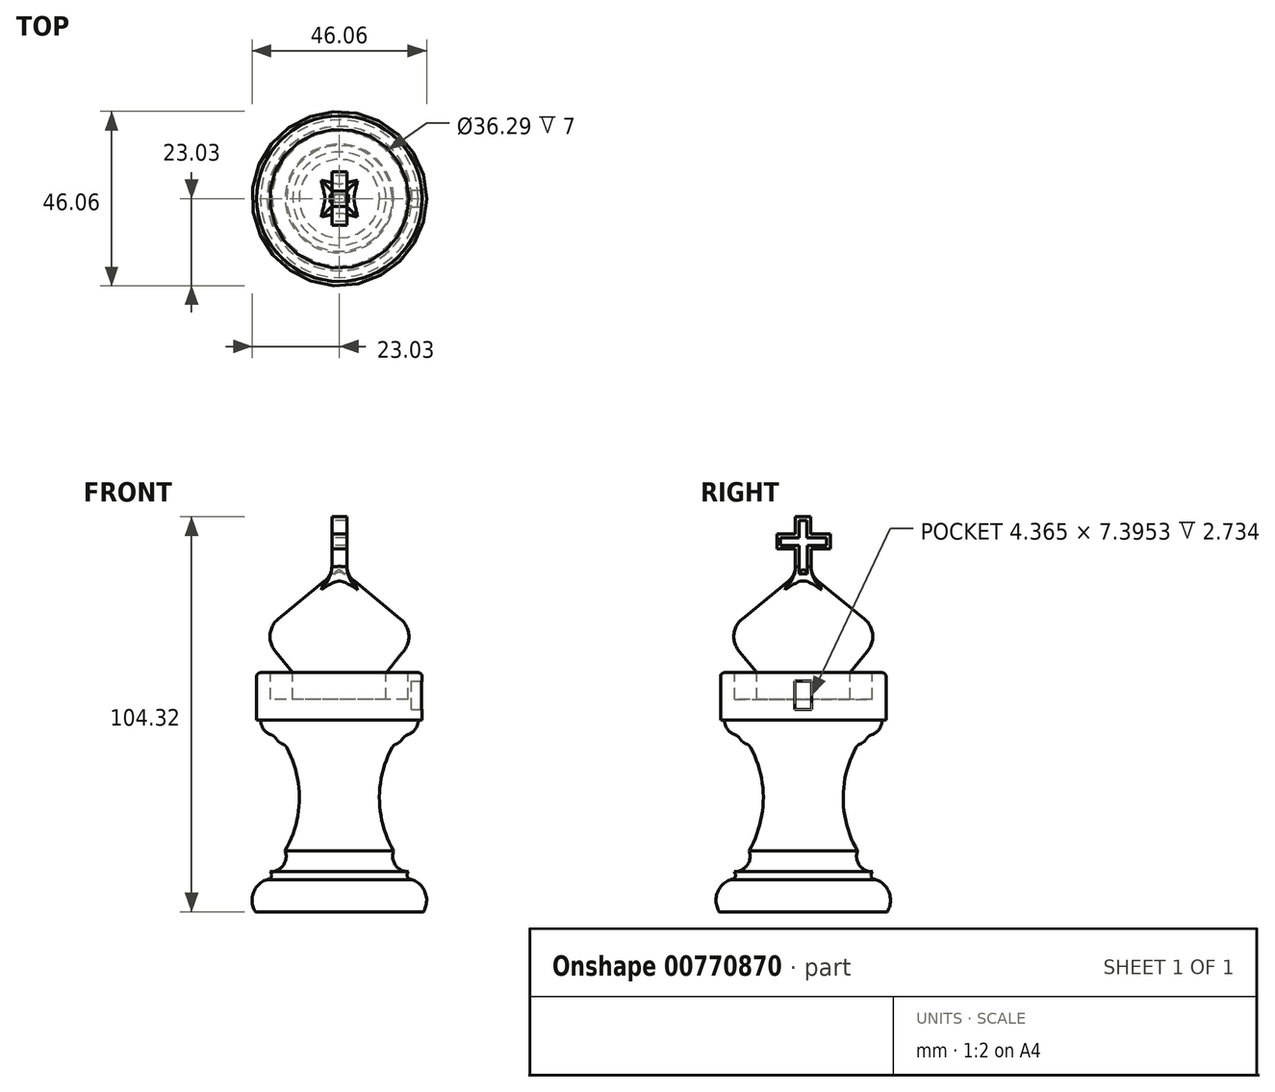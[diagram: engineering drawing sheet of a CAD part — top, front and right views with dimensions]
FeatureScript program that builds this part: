
annotation { "Feature Type Name" : "Feature", "Feature Type Description" : "" }
export const myFeature = defineFeature(function(context is Context, id is Id, definition is map)
    precondition{}
    {
        {
            var Q0;
            Q0=qCreatedBy(makeId("Front.planeOp"),FACE);
            var sketch = newSketch(context, id + "F0", { "sketchPlane" : qUnion([Q0])});
            skLineSegment(sketch, "E0.bottom", {"start": v(0, 0) * mm, "end": v(22.16, 0) * mm});
            skLineSegment(sketch, "E0.top", {"start": v(19.04, 8.54) * mm, "end": v(19.04, 8.54) * mm});
            skLineSegment(sketch, "E1.bottom", {"start": v(19.04, 8.54) * mm, "end": v(19.08, 8.54) * mm});
            skLineSegment(sketch, "E2.bottom", {"start": v(20.81, 50.62) * mm, "end": v(21.84, 50.62) * mm});
            skLineSegment(sketch, "E2.top", {"start": v(12.33, 63.15) * mm, "end": v(21.84, 63.15) * mm});
            skLineSegment(sketch, "E2.right", {"start": v(21.84, 50.62) * mm, "end": v(21.84, 63.15) * mm});
            skLineSegment(sketch, "E3.bottom", {"start": v(12.33, 63.15) * mm, "end": v(20.81, 63.15) * mm});
            skArc(sketch, "E4", {"start": v(14.33, 44.14) * mm, "mid": v(10.55, 30.13) * mm, "end": v(14.33, 16.12) * mm});
            skPoint(sketch, "E5.orphan", {"position": v(9.96, 63.15) * mm});
            skArc(sketch, "E6", {"start": v(18.27, 10.6) * mm, "mid": v(17.95, 9.3) * mm, "end": v(19.04, 8.54) * mm});
            skArc(sketch, "E7", {"start": v(22.16, 0) * mm, "mid": v(22.7, 5.01) * mm, "end": v(19.08, 8.54) * mm});
            skArc(sketch, "E8", {"start": v(14.33, 16.12) * mm, "mid": v(14.82, 12.3) * mm, "end": v(18.27, 10.6) * mm});
            skArc(sketch, "E9", {"start": v(14.33, 44.14) * mm, "mid": v(16.06, 44.95) * mm, "end": v(17.1, 46.54) * mm});
            skArc(sketch, "E10", {"start": v(17.1, 46.54) * mm, "mid": v(19.74, 47.86) * mm, "end": v(20.81, 50.62) * mm});
            skLineSegment(sketch, "E11", {"start": v(0, 90.54) * mm, "end": v(16.13, 77.37) * mm});
            skLineSegment(sketch, "E12", {"start": v(16.99, 68.86) * mm, "end": v(12.33, 63.15) * mm});
            skPoint(sketch, "E13.visualSharp", {"position": v(20.81, 73.55) * mm});
            skArc(sketch, "E13.filletArc", {"start": v(16.99, 68.86) * mm, "mid": v(18.32, 73.3) * mm, "end": v(16.13, 77.37) * mm});
            skPoint(sketch, "E14.orphan", {"position": v(20.81, 83.94) * mm});
            skLineSegment(sketch, "E15", {"start": v(0, 90.54) * mm, "end": v(0, 0) * mm});
            skSolve(sketch);
        }
        {
            var Q0;
            Q0=makeQuery(id+"F0.imprint","IMPRINT",FACE,{"disambiguationData":[TD([[makeQuery(id+"F0.imprint","IMPRINT",EDGE,{"derivedFrom":sQuery(id+"F0.wireOp",EDGE,"E0.bottom")}),1.0]])]});
            var Q1;
            Q1=sQuery(id+"F0.wireOp",EDGE,"E15");
            revolve(context, id + "F1", {"surfaceOperationType" : NewSurfaceOperationType.NEW, "entities" : qUnion([Q0]), "axis" : qUnion([Q1]), "revolveType" : RevolveType.FULL});
        }
        {
            var Q0;
            Q0=makeQuery(id+"F1.opRevolve","SWEPT_EDGE",EDGE,{"disambiguationData":[OSD([sQuery(id+"F0.wireOp",EDGE,"E4"),sQuery(id+"F0.wireOp",EDGE,"E9")])]});
            fillet(context, id + "F2", {"entities" : qUnion([Q0]), "radius" : 2 * mm, "tangentPropagation" : true, "allowEdgeOverflow" : false});
        }
        {
            var Q0;
            Q0=makeQuery(id+"F1.opRevolve","SWEPT_EDGE",EDGE,{"disambiguationData":[OSD([sQuery(id+"F0.wireOp",EDGE,"E9"),sQuery(id+"F0.wireOp",EDGE,"E10")])]});
            fillet(context, id + "F3", {"entities" : qUnion([Q0]), "radius" : 2 * mm, "tangentPropagation" : true, "allowEdgeOverflow" : false});
        }
        {
            var Q0;
            Q0=makeQuery(id+"F1.opRevolve","SWEPT_FACE",FACE,{"disambiguationData":[OSD([sQuery(id+"F0.wireOp",EDGE,"E2.top"),sQuery(id+"F0.wireOp",EDGE,"E3.bottom")])]});
            var sketch = newSketch(context, id + "F4", { "sketchPlane" : qUnion([Q0])});
            skCircle(sketch, "E16", {"center": v(0, 0) * mm, "radius": 18.15 * mm});
            skSolve(sketch);
        }
        {
            var Q0;
            Q0=makeQuery(id+"F4.imprint","IMPRINT",FACE,{"disambiguationData":[TD([[makeQuery(id+"F4.imprint","IMPRINT",EDGE,{"derivedFrom":sQuery(id+"F4.wireOp",EDGE,"E16")}),1.0]])]});
            var Q1;
            Q1=sQuery(id+"F4.wireOp",EDGE,"E16");
            extrude(context, id + "F5", {"entities" : qUnion([Q0]), "operationType" : NewBodyOperationType.REMOVE, "surfaceEntities" : qUnion([Q1]), "oppositeDirection" : true, "depth" : 7 * mm, "offsetDistance" : 25 * mm});
        }
        {
            var Q0;
            Q0=qCreatedBy(makeId("Right.planeOp"),FACE);
            var sketch = newSketch(context, id + "F6", { "sketchPlane" : qUnion([Q0])});
            skLineSegment(sketch, "E17.0", {"start": v(-2.11, 104.32) * mm, "end": v(-2.1, 99.8) * mm});
            skLineSegment(sketch, "E18.0", {"start": v(1.95, 104.32) * mm, "end": v(1.99, 99.8) * mm});
            skLineSegment(sketch, "E19", {"start": v(-2.07, 88.28) * mm, "end": v(2.08, 88.28) * mm});
            skLineSegment(sketch, "E20.0", {"start": v(-7, 95.8) * mm, "end": v(-2.09, 95.8) * mm});
            skLineSegment(sketch, "E21.0", {"start": v(-7, 99.8) * mm, "end": v(-2.1, 99.8) * mm});
            skLineSegment(sketch, "E22.0", {"start": v(-7, 99.8) * mm, "end": v(-7, 95.8) * mm});
            skLineSegment(sketch, "E23.0", {"start": v(7.1, 99.8) * mm, "end": v(7.1, 95.8) * mm});
            skLineSegment(sketch, "E24.0", {"start": v(-2.11, 104.32) * mm, "end": v(1.95, 104.32) * mm});
            skPoint(sketch, "E25.orphan", {"position": v(-10.2, 88.28) * mm});
            skLineSegment(sketch, "E26.trimOffspring", {"start": v(2.02, 95.8) * mm, "end": v(2.08, 88.28) * mm});
            skLineSegment(sketch, "E27.trimOffspring", {"start": v(1.99, 99.8) * mm, "end": v(7.1, 99.8) * mm});
            skLineSegment(sketch, "E28.trimOffspring", {"start": v(-2.09, 95.8) * mm, "end": v(-2.07, 88.28) * mm});
            skLineSegment(sketch, "E29.trimOffspring", {"start": v(2.02, 95.8) * mm, "end": v(7.1, 95.8) * mm});
            skLineSegment(sketch, "E30.0", {"start": v(-6, 96.8) * mm, "end": v(-1.1, 96.8) * mm});
            skLineSegment(sketch, "E30.1", {"start": v(6.1, 98.8) * mm, "end": v(6.1, 96.8) * mm});
            skLineSegment(sketch, "E30.2", {"start": v(1.01, 96.8) * mm, "end": v(6.1, 96.8) * mm});
            skLineSegment(sketch, "E30.3", {"start": v(1.01, 96.8) * mm, "end": v(1.07, 89.28) * mm});
            skLineSegment(sketch, "E30.4", {"start": v(-1.07, 89.28) * mm, "end": v(1.07, 89.28) * mm});
            skLineSegment(sketch, "E30.5", {"start": v(1, 98.8) * mm, "end": v(6.1, 98.8) * mm});
            skLineSegment(sketch, "E30.6", {"start": v(-1.1, 96.8) * mm, "end": v(-1.07, 89.28) * mm});
            skLineSegment(sketch, "E30.7", {"start": v(0.96, 103.32) * mm, "end": v(1, 98.8) * mm});
            skLineSegment(sketch, "E30.8", {"start": v(-1.1, 103.32) * mm, "end": v(0.96, 103.32) * mm});
            skLineSegment(sketch, "E30.9", {"start": v(-1.1, 103.32) * mm, "end": v(-1.1, 98.8) * mm});
            skLineSegment(sketch, "E30.10", {"start": v(-6, 98.8) * mm, "end": v(-1.1, 98.8) * mm});
            skLineSegment(sketch, "E30.11", {"start": v(-6, 98.8) * mm, "end": v(-6, 96.8) * mm});
            skSolve(sketch);
        }
        {
            var Q0;
            Q0=makeQuery(id+"F6.imprint","IMPRINT",FACE,{"disambiguationData":[TD([[makeQuery(id+"F6.imprint","IMPRINT",EDGE,{"derivedFrom":sQuery(id+"F6.wireOp",EDGE,"E17.0")}),1.0]])]});
            extrude(context, id + "F7", {"entities" : qUnion([Q0]), "operationType" : NewBodyOperationType.ADD, "endBound" : BoundingType.SYMMETRIC, "depth" : 4 * mm, "offsetDistance" : 25 * mm});
        }
        {
            var Q0;
            Q0=makeQuery(id+"F7.boolean.opBoolean","INTERSECT",EDGE,{"derivedFrom":[makeQuery(id+"F1.opRevolve","SWEPT_FACE",FACE,{"disambiguationData":[OSD([sQuery(id+"F0.wireOp",EDGE,"E11")])]}),makeQuery(id+"F7.opExtrude","SWEPT_FACE",FACE,{"disambiguationData":[OSD([sQuery(id+"F6.wireOp",EDGE,"E26.trimOffspring")])]})]});
            fillet(context, id + "F8", {"entities" : qUnion([Q0]), "radius" : 5 * mm, "tangentPropagation" : true, "allowEdgeOverflow" : false});
        }
        {
            var Q0;
            Q0=makeQuery(id+"F7.boolean.opBoolean","INTERSECT",EDGE,{"disambiguationData":[OD(0.0)],"derivedFrom":[makeQuery(id+"F1.opRevolve","SWEPT_FACE",FACE,{"disambiguationData":[OSD([sQuery(id+"F0.wireOp",EDGE,"E11")])]}),makeQuery(id+"F7.opExtrude","CAP_FACE",FACE,{"disambiguationData":[OSD([sQuery(id+"F6.wireOp",EDGE,"E17.0"),sQuery(id+"F6.wireOp",EDGE,"E18.0"),sQuery(id+"F6.wireOp",EDGE,"E19"),sQuery(id+"F6.wireOp",EDGE,"E20.0"),sQuery(id+"F6.wireOp",EDGE,"E21.0"),sQuery(id+"F6.wireOp",EDGE,"E22.0"),sQuery(id+"F6.wireOp",EDGE,"E23.0"),sQuery(id+"F6.wireOp",EDGE,"E24.0"),sQuery(id+"F6.wireOp",EDGE,"E26.trimOffspring"),sQuery(id+"F6.wireOp",EDGE,"E27.trimOffspring"),sQuery(id+"F6.wireOp",EDGE,"E28.trimOffspring"),sQuery(id+"F6.wireOp",EDGE,"E29.trimOffspring"),sQuery(id+"F6.wireOp",EDGE,"E30.0"),sQuery(id+"F6.wireOp",EDGE,"E30.1"),sQuery(id+"F6.wireOp",EDGE,"E30.2"),sQuery(id+"F6.wireOp",EDGE,"E30.3"),sQuery(id+"F6.wireOp",EDGE,"E30.4"),sQuery(id+"F6.wireOp",EDGE,"E30.5"),sQuery(id+"F6.wireOp",EDGE,"E30.6"),sQuery(id+"F6.wireOp",EDGE,"E30.7"),sQuery(id+"F6.wireOp",EDGE,"E30.8"),sQuery(id+"F6.wireOp",EDGE,"E30.9"),sQuery(id+"F6.wireOp",EDGE,"E30.10"),sQuery(id+"F6.wireOp",EDGE,"E30.11")])],"isStart":false})]});
            fillet(context, id + "F9", {"entities" : qUnion([Q0]), "radius" : 5 * mm, "tangentPropagation" : true, "allowEdgeOverflow" : false});
        }
        {
            var Q0;
            Q0=makeQuery(id+"F7.boolean.opBoolean","INTERSECT",EDGE,{"disambiguationData":[OD(0.0)],"derivedFrom":[makeQuery(id+"F1.opRevolve","SWEPT_FACE",FACE,{"disambiguationData":[OSD([sQuery(id+"F0.wireOp",EDGE,"E11")])]}),makeQuery(id+"F7.opExtrude","CAP_FACE",FACE,{"disambiguationData":[OSD([sQuery(id+"F6.wireOp",EDGE,"E17.0"),sQuery(id+"F6.wireOp",EDGE,"E18.0"),sQuery(id+"F6.wireOp",EDGE,"E19"),sQuery(id+"F6.wireOp",EDGE,"E20.0"),sQuery(id+"F6.wireOp",EDGE,"E21.0"),sQuery(id+"F6.wireOp",EDGE,"E22.0"),sQuery(id+"F6.wireOp",EDGE,"E23.0"),sQuery(id+"F6.wireOp",EDGE,"E24.0"),sQuery(id+"F6.wireOp",EDGE,"E26.trimOffspring"),sQuery(id+"F6.wireOp",EDGE,"E27.trimOffspring"),sQuery(id+"F6.wireOp",EDGE,"E28.trimOffspring"),sQuery(id+"F6.wireOp",EDGE,"E29.trimOffspring"),sQuery(id+"F6.wireOp",EDGE,"E30.0"),sQuery(id+"F6.wireOp",EDGE,"E30.1"),sQuery(id+"F6.wireOp",EDGE,"E30.2"),sQuery(id+"F6.wireOp",EDGE,"E30.3"),sQuery(id+"F6.wireOp",EDGE,"E30.4"),sQuery(id+"F6.wireOp",EDGE,"E30.5"),sQuery(id+"F6.wireOp",EDGE,"E30.6"),sQuery(id+"F6.wireOp",EDGE,"E30.7"),sQuery(id+"F6.wireOp",EDGE,"E30.8"),sQuery(id+"F6.wireOp",EDGE,"E30.9"),sQuery(id+"F6.wireOp",EDGE,"E30.10"),sQuery(id+"F6.wireOp",EDGE,"E30.11")])],"isStart":true})]});
            fillet(context, id + "F10", {"entities" : qUnion([Q0]), "radius" : 5 * mm, "tangentPropagation" : true, "allowEdgeOverflow" : false});
        }
        {
            var Q0;
            Q0=makeQuery(id+"F7.boolean.opBoolean","INTERSECT",EDGE,{"derivedFrom":[makeQuery(id+"F1.opRevolve","SWEPT_FACE",FACE,{"disambiguationData":[OSD([sQuery(id+"F0.wireOp",EDGE,"E11")])]}),makeQuery(id+"F7.opExtrude","SWEPT_FACE",FACE,{"disambiguationData":[OSD([sQuery(id+"F6.wireOp",EDGE,"E28.trimOffspring")])]})]});
            fillet(context, id + "F11", {"entities" : qUnion([Q0]), "radius" : 5 * mm, "tangentPropagation" : true, "allowEdgeOverflow" : false});
        }
        {
            var Q0;
            Q0=makeQuery(id+"F1.opRevolve","SWEPT_EDGE",EDGE,{"disambiguationData":[OSD([sQuery(id+"F0.wireOp",EDGE,"E2.top"),sQuery(id+"F0.wireOp",EDGE,"E2.right")])]});
            fillet(context, id + "F12", {"entities" : qUnion([Q0]), "radius" : 1 * mm, "tangentPropagation" : true, "allowEdgeOverflow" : false});
        }
        {
            var Q0;
            Q0=qCreatedBy(makeId("Right.planeOp"),FACE);
            cPlane(context, id + "F13", {"entities" : qUnion([Q0]), "cplaneType" : CPlaneType.OFFSET, "offset" : 25 * mm, "width" : 150 * mm, "height" : 150 * mm});
        }
        {
            var Q0;
            Q0=qCreatedBy(id+"F13.planeOp",FACE);
            var sketch = newSketch(context, id + "F14", { "sketchPlane" : qUnion([Q0])});
            skLineSegment(sketch, "E31.bottom", {"start": v(2.18, 53.47) * mm, "end": v(-2.18, 53.47) * mm});
            skLineSegment(sketch, "E31.top", {"start": v(2.18, 60.87) * mm, "end": v(-2.18, 60.87) * mm});
            skLineSegment(sketch, "E31.left", {"start": v(2.18, 53.47) * mm, "end": v(2.18, 60.87) * mm});
            skLineSegment(sketch, "E31.right", {"start": v(-2.18, 53.47) * mm, "end": v(-2.18, 60.87) * mm});
            skPoint(sketch, "E31.middle", {"position": v(0, 57.17) * mm});
            skSolve(sketch);
        }
        {
            var Q0;
            Q0 = qSketchRegion(id + "F14", true);
            extrude(context, id + "F15", {"entities" : qUnion([Q0]), "operationType" : NewBodyOperationType.REMOVE, "oppositeDirection" : true, "depth" : 6 * mm, "offsetDistance" : 25 * mm});
        }
    });
